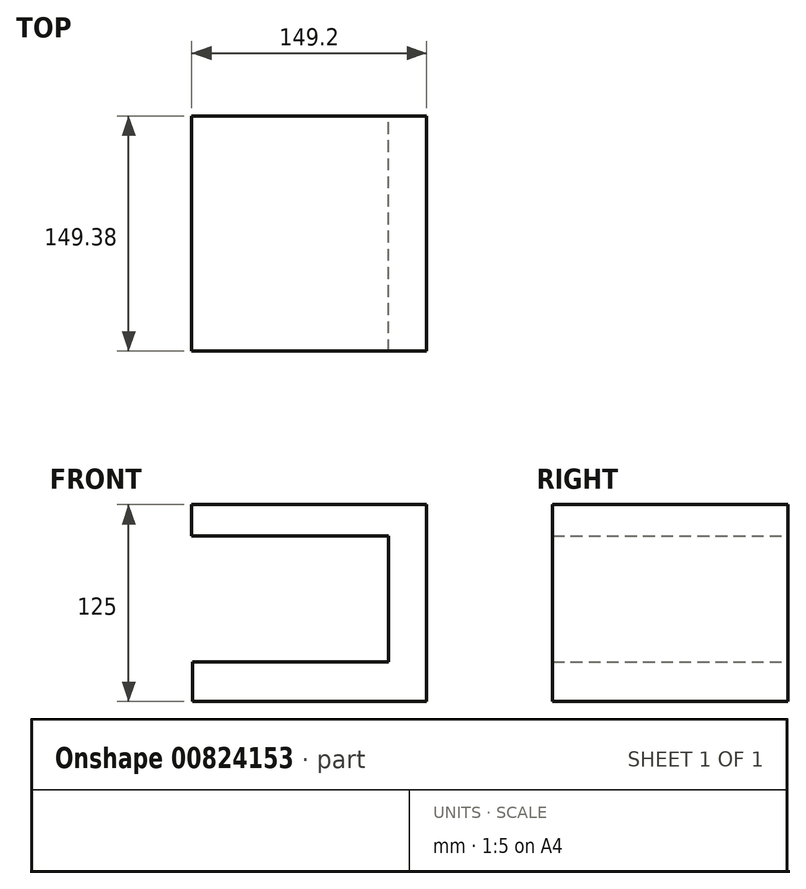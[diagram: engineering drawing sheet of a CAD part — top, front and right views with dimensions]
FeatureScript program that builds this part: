
annotation { "Feature Type Name" : "Feature", "Feature Type Description" : "" }
export const myFeature = defineFeature(function(context is Context, id is Id, definition is map)
    precondition{}
    {
        {
            var Q0;
            Q0=qCreatedBy(makeId("Top.planeOp"),FACE);
            var sketch = newSketch(context, id + "F0", { "sketchPlane" : qUnion([Q0])});
            skLineSegment(sketch, "E0.bottom", {"start": v(-74.38, -74.7) * mm, "end": v(74.38, -74.7) * mm});
            skLineSegment(sketch, "E0.top", {"start": v(-74.38, 74.7) * mm, "end": v(74.38, 74.7) * mm});
            skLineSegment(sketch, "E0.left", {"start": v(-74.38, -74.7) * mm, "end": v(-74.38, 74.7) * mm});
            skLineSegment(sketch, "E0.right", {"start": v(74.38, -74.7) * mm, "end": v(74.38, 74.7) * mm});
            skPoint(sketch, "E0.middle", {"position": v(0, 0) * mm});
            skSolve(sketch);
        }
        {
            var Q0;
            Q0=makeQuery(id+"F0.imprint","IMPRINT",FACE,{"disambiguationData":[TD([[makeQuery(id+"F0.imprint","IMPRINT",EDGE,{"derivedFrom":sQuery(id+"F0.wireOp",EDGE,"E0.bottom")}),1.0]])]});
            extrude(context, id + "F1", {"entities" : qUnion([Q0]), "depth" : 25 * mm, "offsetDistance" : 25 * mm});
        }
        {
            var Q0;
            Q0=makeQuery(id+"F1.opExtrude","CAP_FACE",FACE,{"disambiguationData":[OSD([sQuery(id+"F0.wireOp",EDGE,"E0.bottom"),sQuery(id+"F0.wireOp",EDGE,"E0.top"),sQuery(id+"F0.wireOp",EDGE,"E0.left"),sQuery(id+"F0.wireOp",EDGE,"E0.right")])],"isStart":false});
            var sketch = newSketch(context, id + "F2", { "sketchPlane" : qUnion([Q0])});
            skLineSegment(sketch, "E1.bottom", {"start": v(74.38, -74.7) * mm, "end": v(50.18, -74.7) * mm});
            skLineSegment(sketch, "E1.top", {"start": v(74.38, 74.7) * mm, "end": v(50.18, 74.7) * mm});
            skLineSegment(sketch, "E1.left", {"start": v(74.38, -74.7) * mm, "end": v(74.38, 74.7) * mm});
            skLineSegment(sketch, "E1.right", {"start": v(50.18, -74.7) * mm, "end": v(50.18, 74.7) * mm});
            skSolve(sketch);
        }
        {
            var Q0;
            Q0=makeQuery(id+"F2.imprint","IMPRINT",FACE,{"disambiguationData":[TD([[makeQuery(id+"F2.imprint","IMPRINT",EDGE,{"derivedFrom":sQuery(id+"F2.wireOp",EDGE,"E1.bottom")}),1.0]])]});
            extrude(context, id + "F3", {"entities" : qUnion([Q0]), "operationType" : NewBodyOperationType.ADD, "depth" : 100 * mm, "offsetDistance" : 25 * mm});
        }
        {
            var Q0;
            Q0=makeQuery(id+"F3.opExtrude","SWEPT_FACE",FACE,{"disambiguationData":[OSD([sQuery(id+"F2.wireOp",EDGE,"E1.right")])]});
            var sketch = newSketch(context, id + "F4", { "sketchPlane" : qUnion([Q0])});
            skLineSegment(sketch, "E2", {"start": v(74.7, 105.04) * mm, "end": v(-74.7, 105.04) * mm});
            skSolve(sketch);
        }
        {
            var Q0;
            {var subQ0=sQuery(id+"F4.wireOp",EDGE,"E2");Q0=makeQuery(id+"F4.imprint","IMPRINT",FACE,{"disambiguationData":[TD([[makeQuery(id+"F4.imprint","IMPRINT",EDGE,{"derivedFrom":subQ0}),-1.0]])]});}
            extrude(context, id + "F5", {"entities" : qUnion([Q0]), "operationType" : NewBodyOperationType.ADD, "depth" : 125 * mm, "offsetDistance" : 25 * mm});
        }
    });
